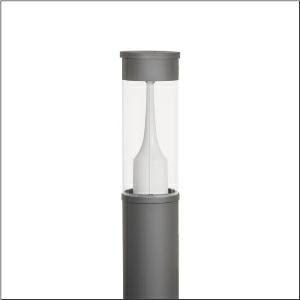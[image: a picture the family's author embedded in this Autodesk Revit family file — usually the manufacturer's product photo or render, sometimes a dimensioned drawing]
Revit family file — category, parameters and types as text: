
# Revit family: city-light_260_iq___st1_2a_5xa5295kf14h_47e0
name_source: partatom
category: Lighting Fixtures
units: mm (PartAtom-declared; Revit-internal decimal feet)

## family parameters
Cut with Voids When Loaded = No
Host = Face
Light Source = No
Part Type = Normal
Room Calculation Point = No
Round Connector Dimension = Use Diameter
Shared = No

## types (1)
- --- (1 x LED, 1540 lm, 10 W, 4000K)
    Apparent Load = 10 VA
    CIE Flux Codes = 22 61 93 96 100
    Color Rendering = 70
    Color Temperature = 4000K
    Default Elevation = 1800 mm
    Description = City-Light 260 iQ, light pillar, Module 540 iQ-SR, primary light control with 3 zone facetted reflector, of plastic, silver coated, highly specular, structured, primary optical cover: cover, of PMMA, transparent, partly coated, light distribution: ST1.2a, primary light characteristic: asymmetric, LED, High Power LED, rated luminous flux: 1.540lm, luminous efficacy: 154lm/W, light colour: 740, colour temperature: 4000K, control gear: ECG iQ, control: presetting dimming logarithmic, Street-Remote, Auto-Match, Temp-Guard, Lumen-Switch, Night-Set, Smart-Wire, Light-Fading, Desk-Remote (wireless, voltage-free reading and setting of iQ features in the workshop via application-optimized NFC function/RFID function), optimised constant luminous flux control (CLO 2.0), with terminal, 6-pole, max. 2.5mm², mains connection: 230..240V, AC, 50/60Hz, start of lifetime: 10W, end of service life: 10W, reduction: 5W, luminaire housing, cylindrical, of extruded aluminium section, coated, Siteco® metallic grey (DB 702S), length: 2.600mm, diameter: 200mm, Module 540 iQ-SR, traffic white (RAL 9016), equipment: standard, protection rating (complete): IP65, insulation class (complete): insulation class II (safety insulation), certification: CE, ENEC, VDE, packaging unit: 1 piece

Light Distribution: ST1.2a
    Height = 500 mm
    Lamp = 1 x LED
    Lamp Light Flux = 1540 lm
    Lamp Power = 10 W
    Lamp count = 1
    Length = 200 mm  [stored 0.656168 ft]
    Luminous efficacy = 154 lm/W
    Manufacturer = Siteco
    ModVariant = No
    Model = 5XA5295KF14H
    Mounting Place = Floor
    Mounting Type = Freestanding
    Number of Poles = 1
    OnlyDefault = Yes
    Power Factor = 1
    Product Name = City-Light 260 iQ | ST1.2a
    Product group = light pillar
    ProductGroupID = 1303
    Protection Class = Protection class II
    Protection Degree = IP 65
    RLX_Detail_Level = 1
    RLX_Emergency_Light_Flux = 0 lm
    RLX_Emergency_Type = 0
    RLX_Emergency_Type_DB = No
    RlxData = <blob elided: 64801 chars, md5=bfe24d8c>
    Socket = socket
    Standby Power = 0 W
    System Light Flux = 1540 lm
    System Power = 10 W
    Type Comments = factory setting: luminous flux: 100 % | dim-lin: 254 | 401 mA
    Type Image = l_1006918.jpg
    URL = http://relux.com
    VarID = @adj_091495
    Voltage = 0 V
    Weight = 0.00 kg
    Width = 0 mm  [stored 0 ft]

note: [stored X ft] marks values corroborated as IEEE doubles in the binary element streams (Revit-internal decimal feet)

## geometry (parser evidence)
native form markers: Blend x4, Sweep x11
no freeform markers — native parametric forms only
